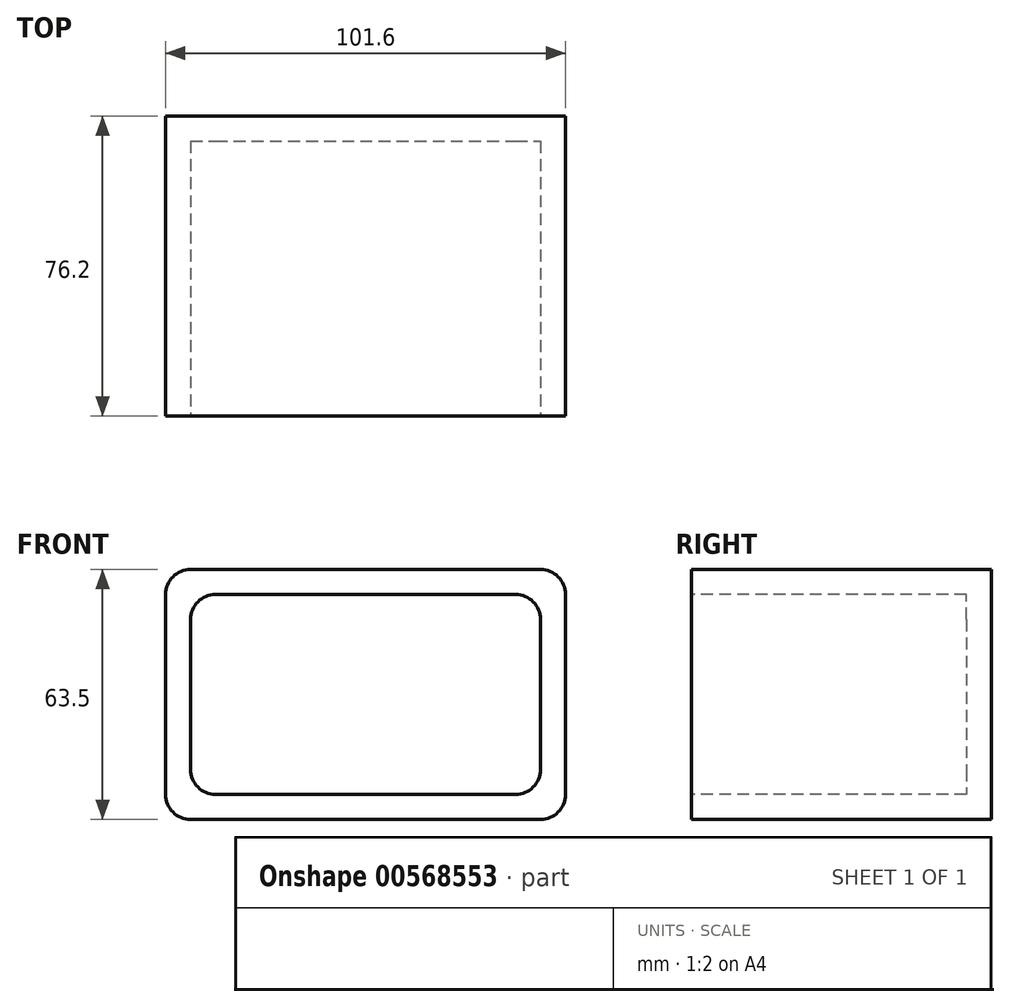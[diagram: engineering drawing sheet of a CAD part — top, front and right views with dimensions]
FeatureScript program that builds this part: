
annotation { "Feature Type Name" : "Feature", "Feature Type Description" : "" }
export const myFeature = defineFeature(function(context is Context, id is Id, definition is map)
    precondition{}
    {
        {
            var Q0;
            Q0=qCreatedBy(makeId("Front.planeOp"),FACE);
            var sketch = newSketch(context, id + "F0", { "sketchPlane" : qUnion([Q0])});
            skLineSegment(sketch, "E0.bottom", {"start": v(-69.53, 24.16) * mm, "end": v(19.37, 24.16) * mm});
            skLineSegment(sketch, "E0.top", {"start": v(-69.53, -39.34) * mm, "end": v(19.37, -39.34) * mm});
            skLineSegment(sketch, "E0.left", {"start": v(-75.88, 17.81) * mm, "end": v(-75.88, -32.99) * mm});
            skLineSegment(sketch, "E0.right", {"start": v(25.72, 17.81) * mm, "end": v(25.72, -32.99) * mm});
            skArc(sketch, "E1.filletArc", {"start": v(-69.53, 24.16) * mm, "mid": v(-74.02, 22.3) * mm, "end": v(-75.88, 17.81) * mm});
            skArc(sketch, "E2.filletArc", {"start": v(-75.88, -32.99) * mm, "mid": v(-74.02, -37.48) * mm, "end": v(-69.53, -39.34) * mm});
            skPoint(sketch, "E3.visualSharp", {"position": v(25.72, -39.34) * mm});
            skArc(sketch, "E3.filletArc", {"start": v(19.37, -39.34) * mm, "mid": v(23.86, -37.48) * mm, "end": v(25.72, -32.99) * mm});
            skArc(sketch, "E4.filletArc", {"start": v(25.72, 17.81) * mm, "mid": v(23.86, 22.3) * mm, "end": v(19.37, 24.16) * mm});
            skSolve(sketch);
        }
        {
            var Q0;
            Q0=makeQuery(id+"F0.imprint","IMPRINT",FACE,{"disambiguationData":[TD([[makeQuery(id+"F0.imprint","IMPRINT",EDGE,{"derivedFrom":sQuery(id+"F0.wireOp",EDGE,"E0.bottom")}),-1.0]])]});
            extrude(context, id + "F1", {"entities" : qUnion([Q0]), "oppositeDirection" : true, "depth" : 76.2 * mm, "offsetDistance" : 25.4 * mm});
        }
        {
            var Q0;
            Q0=makeQuery(id+"F1.opExtrude","CAP_FACE",FACE,{"disambiguationData":[OSD([sQuery(id+"F0.wireOp",EDGE,"E0.bottom"),sQuery(id+"F0.wireOp",EDGE,"E0.top"),sQuery(id+"F0.wireOp",EDGE,"E0.left"),sQuery(id+"F0.wireOp",EDGE,"E0.right"),sQuery(id+"F0.wireOp",EDGE,"E1.filletArc"),sQuery(id+"F0.wireOp",EDGE,"E2.filletArc"),sQuery(id+"F0.wireOp",EDGE,"E3.filletArc"),sQuery(id+"F0.wireOp",EDGE,"E4.filletArc")])],"isStart":true});
            var sketch = newSketch(context, id + "F2", { "sketchPlane" : qUnion([Q0])});
            skLineSegment(sketch, "E5.bottom", {"start": v(-63.18, 17.81) * mm, "end": v(13.02, 17.81) * mm});
            skLineSegment(sketch, "E5.top", {"start": v(-63.18, -32.99) * mm, "end": v(13.02, -32.99) * mm});
            skLineSegment(sketch, "E5.left", {"start": v(-69.53, 11.46) * mm, "end": v(-69.53, -26.64) * mm});
            skLineSegment(sketch, "E5.right", {"start": v(19.37, 11.46) * mm, "end": v(19.37, -26.64) * mm});
            skPoint(sketch, "E6.visualSharp", {"position": v(-69.53, 17.81) * mm});
            skArc(sketch, "E6.filletArc", {"start": v(-63.18, 17.81) * mm, "mid": v(-67.67, 15.95) * mm, "end": v(-69.53, 11.46) * mm});
            skPoint(sketch, "E7.visualSharp", {"position": v(-69.53, -32.99) * mm});
            skArc(sketch, "E7.filletArc", {"start": v(-69.53, -26.64) * mm, "mid": v(-67.67, -31.13) * mm, "end": v(-63.18, -32.99) * mm});
            skPoint(sketch, "E8.visualSharp", {"position": v(19.37, -32.99) * mm});
            skArc(sketch, "E8.filletArc", {"start": v(13.02, -32.99) * mm, "mid": v(17.51, -31.13) * mm, "end": v(19.37, -26.64) * mm});
            skPoint(sketch, "E9.visualSharp", {"position": v(19.37, 17.81) * mm});
            skArc(sketch, "E9.filletArc", {"start": v(19.37, 11.46) * mm, "mid": v(17.51, 15.95) * mm, "end": v(13.02, 17.81) * mm});
            skSolve(sketch);
        }
        {
            var Q0;
            Q0=makeQuery(id+"F2.imprint","IMPRINT",FACE,{"disambiguationData":[TD([[makeQuery(id+"F2.imprint","IMPRINT",EDGE,{"derivedFrom":sQuery(id+"F2.wireOp",EDGE,"E5.bottom")}),-1.0]])]});
            extrude(context, id + "F3", {"entities" : qUnion([Q0]), "operationType" : NewBodyOperationType.REMOVE, "oppositeDirection" : true, "depth" : 69.85 * mm, "offsetDistance" : 25.4 * mm});
        }
    });
